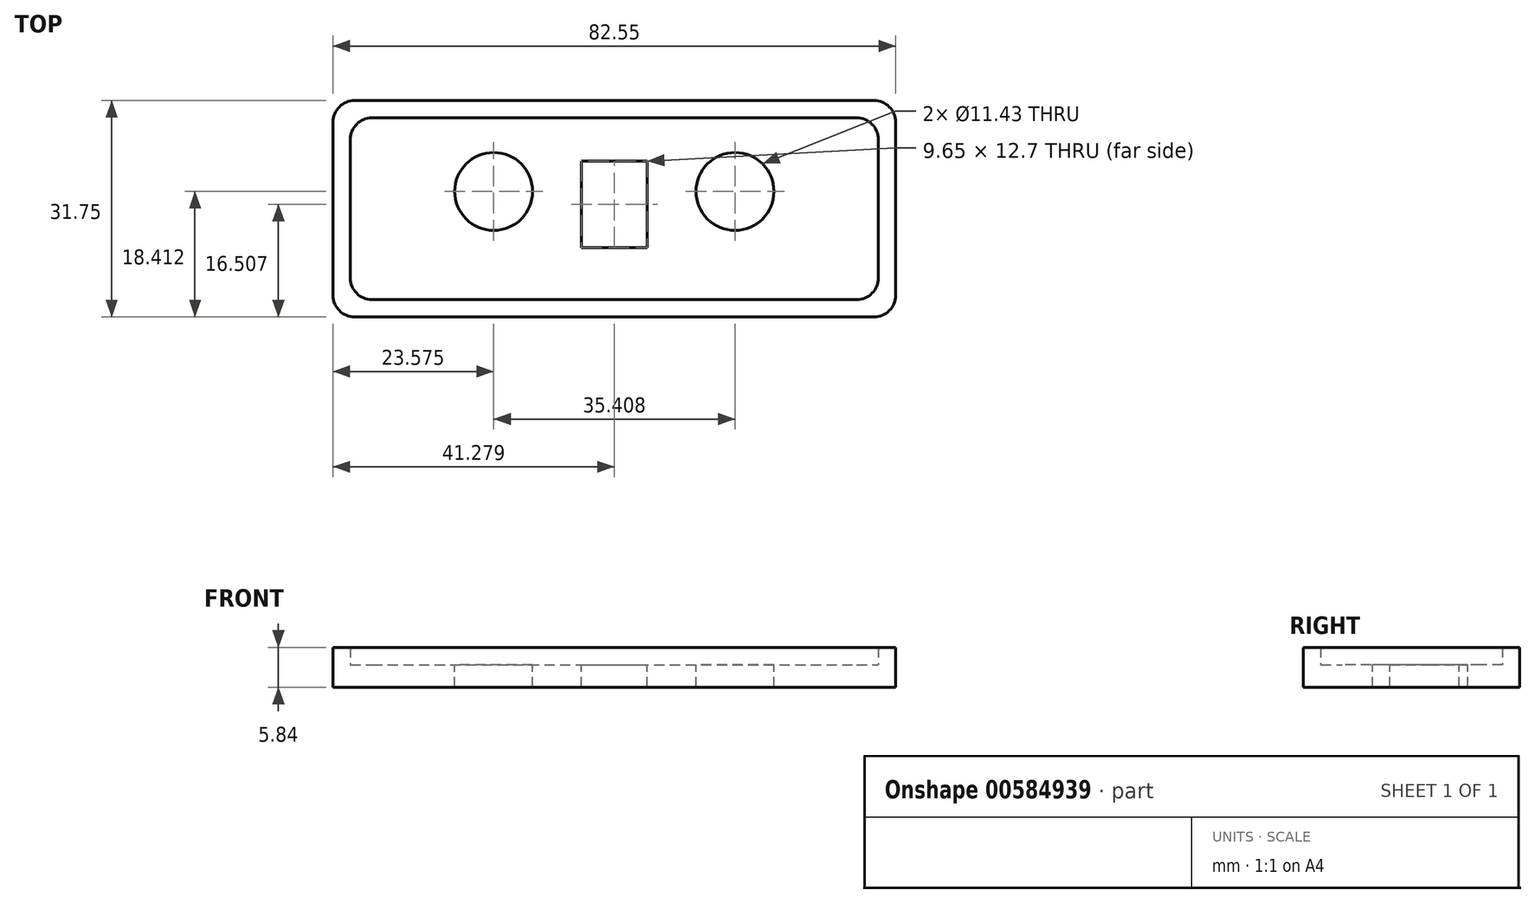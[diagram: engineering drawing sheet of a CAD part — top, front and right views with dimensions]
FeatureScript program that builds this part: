
annotation { "Feature Type Name" : "Feature", "Feature Type Description" : "" }
export const myFeature = defineFeature(function(context is Context, id is Id, definition is map)
    precondition{}
    {
        {
            var Q0;
            Q0=qCreatedBy(makeId("Top.planeOp"),FACE);
            var sketch = newSketch(context, id + "F0", { "sketchPlane" : qUnion([Q0])});
            skLineSegment(sketch, "E0.bottom", {"start": v(12.86, -33.07) * mm, "end": v(83.98, -33.07) * mm});
            skLineSegment(sketch, "E0.top", {"start": v(12.86, -6.4) * mm, "end": v(83.98, -6.4) * mm});
            skLineSegment(sketch, "E0.left", {"start": v(9.68, -9.58) * mm, "end": v(9.68, -29.9) * mm});
            skLineSegment(sketch, "E0.right", {"start": v(87.15, -9.58) * mm, "end": v(87.15, -29.9) * mm});
            skPoint(sketch, "E1", {"position": v(48.42, -6.4) * mm});
            skPoint(sketch, "E2", {"position": v(9.68, -19.74) * mm});
            skLineSegment(sketch, "E3.0", {"start": v(10.32, -3.86) * mm, "end": v(86.52, -3.86) * mm});
            skLineSegment(sketch, "E3.1", {"start": v(7.14, -7.04) * mm, "end": v(7.14, -32.44) * mm});
            skLineSegment(sketch, "E3.2", {"start": v(10.32, -35.61) * mm, "end": v(86.52, -35.61) * mm});
            skLineSegment(sketch, "E3.3", {"start": v(89.7, -7.04) * mm, "end": v(89.7, -32.44) * mm});
            skPoint(sketch, "E4.visualSharp", {"position": v(87.15, -33.07) * mm});
            skArc(sketch, "E4.filletArc", {"start": v(83.98, -33.07) * mm, "mid": v(86.22, -32.14) * mm, "end": v(87.15, -29.9) * mm});
            skPoint(sketch, "E5.visualSharp", {"position": v(87.15, -6.4) * mm});
            skArc(sketch, "E5.filletArc", {"start": v(87.15, -9.58) * mm, "mid": v(86.22, -7.33) * mm, "end": v(83.98, -6.4) * mm});
            skPoint(sketch, "E6.visualSharp", {"position": v(89.7, -35.61) * mm});
            skArc(sketch, "E6.filletArc", {"start": v(86.52, -35.61) * mm, "mid": v(88.76, -34.68) * mm, "end": v(89.7, -32.44) * mm});
            skPoint(sketch, "E7.visualSharp", {"position": v(89.7, -3.86) * mm});
            skArc(sketch, "E7.filletArc", {"start": v(89.7, -7.04) * mm, "mid": v(88.76, -4.8) * mm, "end": v(86.52, -3.86) * mm});
            skPoint(sketch, "E8.visualSharp", {"position": v(9.68, -33.07) * mm});
            skArc(sketch, "E8.filletArc", {"start": v(9.68, -29.9) * mm, "mid": v(10.61, -32.14) * mm, "end": v(12.86, -33.07) * mm});
            skPoint(sketch, "E9.visualSharp", {"position": v(7.14, -35.61) * mm});
            skArc(sketch, "E9.filletArc", {"start": v(7.14, -32.44) * mm, "mid": v(8.07, -34.68) * mm, "end": v(10.32, -35.61) * mm});
            skPoint(sketch, "E10.visualSharp", {"position": v(7.14, -3.86) * mm});
            skArc(sketch, "E10.filletArc", {"start": v(10.32, -3.86) * mm, "mid": v(8.07, -4.8) * mm, "end": v(7.14, -7.04) * mm});
            skPoint(sketch, "E11.visualSharp", {"position": v(9.68, -6.4) * mm});
            skArc(sketch, "E11.filletArc", {"start": v(12.86, -6.4) * mm, "mid": v(10.61, -7.33) * mm, "end": v(9.68, -9.58) * mm});
            skSolve(sketch);
        }
        {
            var Q0;
            Q0=makeQuery(id+"F0.imprint","IMPRINT",FACE,{"disambiguationData":[TD([[makeQuery(id+"F0.imprint","IMPRINT",EDGE,{"derivedFrom":sQuery(id+"F0.wireOp",EDGE,"E0.bottom")}),-1.0]])]});
            var Q1;
            Q1=makeQuery(id+"F0.imprint","IMPRINT",FACE,{"disambiguationData":[TD([[makeQuery(id+"F0.imprint","IMPRINT",EDGE,{"derivedFrom":sQuery(id+"F0.wireOp",EDGE,"E0.bottom")}),1.0]])]});
            extrude(context, id + "F1", {"entities" : qUnion([Q0, Q1]), "oppositeDirection" : true, "depth" : 3.3 * mm, "offsetDistance" : 25.4 * mm});
        }
        {
            var Q0;
            Q0=makeQuery(id+"F0.imprint","IMPRINT",FACE,{"disambiguationData":[TD([[makeQuery(id+"F0.imprint","IMPRINT",EDGE,{"derivedFrom":sQuery(id+"F0.wireOp",EDGE,"E0.bottom")}),-1.0]])]});
            extrude(context, id + "F2", {"entities" : qUnion([Q0]), "operationType" : NewBodyOperationType.ADD, "depth" : 2.54 * mm, "offsetDistance" : 25.4 * mm});
        }
        {
            var Q0;
            Q0=qCreatedBy(makeId("Top.planeOp"),FACE);
            var sketch = newSketch(context, id + "F3", { "sketchPlane" : qUnion([Q0])});
            skCircle(sketch, "E12", {"center": v(30.72, -17.2) * mm, "radius": 5.72 * mm});
            skCircle(sketch, "E13", {"center": v(66.12, -17.2) * mm, "radius": 5.72 * mm});
            skLineSegment(sketch, "E14.bottom", {"start": v(43.6, -12.75) * mm, "end": v(53.24, -12.75) * mm});
            skLineSegment(sketch, "E14.top", {"start": v(43.6, -25.45) * mm, "end": v(53.24, -25.45) * mm});
            skLineSegment(sketch, "E14.left", {"start": v(43.6, -12.75) * mm, "end": v(43.6, -25.45) * mm});
            skLineSegment(sketch, "E14.right", {"start": v(53.24, -12.75) * mm, "end": v(53.24, -25.45) * mm});
            skPoint(sketch, "E15", {"position": v(48.42, -12.75) * mm});
            skLineSegment(sketch, "E16", {"start": v(30.72, -17.2) * mm, "end": v(66.12, -17.2) * mm});
            skPoint(sketch, "E17", {"position": v(48.42, -17.2) * mm});
            skSolve(sketch);
        }
        {
            var Q0;
            Q0=qSketchRegion(id+"F3",true);
            extrude(context, id + "F4", {"entities" : qUnion([Q0]), "operationType" : NewBodyOperationType.REMOVE, "endBound" : BoundingType.THROUGH_ALL, "oppositeDirection" : true, "depth" : 25.4 * mm, "offsetDistance" : 25.4 * mm});
        }
    });
